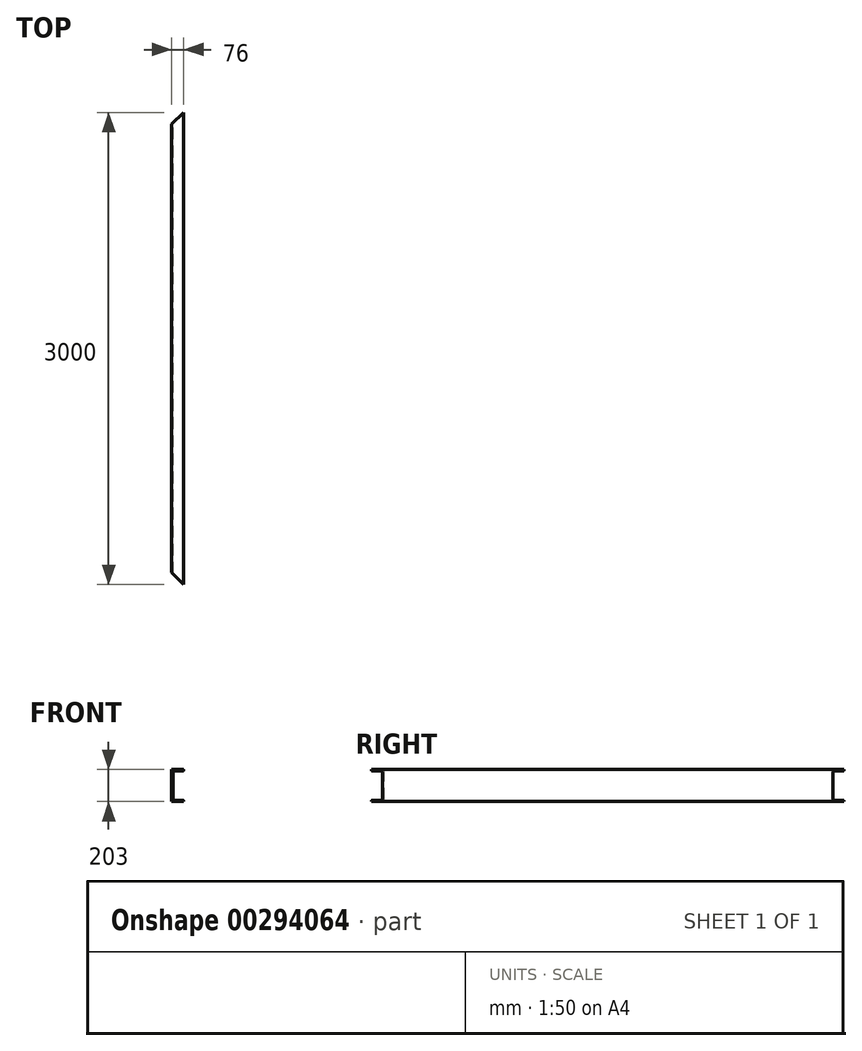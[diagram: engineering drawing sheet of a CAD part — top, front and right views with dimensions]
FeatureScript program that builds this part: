
annotation { "Feature Type Name" : "Feature", "Feature Type Description" : "" }
export const myFeature = defineFeature(function(context is Context, id is Id, definition is map)
    precondition{}
    {
        {
            var Q0;
            Q0=qCreatedBy(makeId("Front.planeOp"),FACE);
            var sketch = newSketch(context, id + "F0", { "sketchPlane" : qUnion([Q0])});
            skLineSegment(sketch, "E0", {"start": v(-38, 101.5) * mm, "end": v(-38, -101.5) * mm});
            skLineSegment(sketch, "E1", {"start": v(-38, -101.5) * mm, "end": v(38, -101.5) * mm});
            skLineSegment(sketch, "E2", {"start": v(38, -101.5) * mm, "end": v(38, -98.1) * mm});
            skArc(sketch, "E3", {"start": v(38, -98.1) * mm, "mid": v(36.63, -94.66) * mm, "end": v(33.27, -93.1) * mm});
            skLineSegment(sketch, "E4", {"start": v(33.27, -93.1) * mm, "end": v(-21.44, -90.17) * mm});
            skArc(sketch, "E5", {"start": v(-21.44, -90.17) * mm, "mid": v(-28.16, -87.07) * mm, "end": v(-30.9, -80.19) * mm});
            skLineSegment(sketch, "E6", {"start": v(-30.9, -80.19) * mm, "end": v(-30.9, 80.19) * mm});
            skArc(sketch, "E7", {"start": v(-30.9, 80.19) * mm, "mid": v(-28.16, 87.07) * mm, "end": v(-21.44, 90.17) * mm});
            skLineSegment(sketch, "E8", {"start": v(-21.44, 90.17) * mm, "end": v(33.27, 93.1) * mm});
            skArc(sketch, "E9", {"start": v(33.27, 93.1) * mm, "mid": v(36.63, 94.66) * mm, "end": v(38, 98.1) * mm});
            skLineSegment(sketch, "E10", {"start": v(38, 98.1) * mm, "end": v(38, 101.5) * mm});
            skLineSegment(sketch, "E11", {"start": v(38, 101.5) * mm, "end": v(-38, 101.5) * mm});
            skSolve(sketch);
        }
        {
            var Q0;
            Q0=makeQuery(id+"F0.imprint","IMPRINT",FACE,{"disambiguationData":[TD([[makeQuery(id+"F0.imprint","IMPRINT",EDGE,{"derivedFrom":sQuery(id+"F0.wireOp",EDGE,"E0")}),1.0]])]});
            extrude(context, id + "F1", {"entities" : qUnion([Q0]), "depth" : 3000 * mm});
        }
        {
            var Q0;
            Q0=qCreatedBy(makeId("Top.planeOp"),FACE);
            var sketch = newSketch(context, id + "F2", { "sketchPlane" : qUnion([Q0])});
            skLineSegment(sketch, "E12", {"start": v(-38, 0) * mm, "end": v(-38, -76) * mm});
            skLineSegment(sketch, "E13", {"start": v(38, 0) * mm, "end": v(-38, -76) * mm});
            skLineSegment(sketch, "E14", {"start": v(38, 0) * mm, "end": v(-38, 0) * mm});
            skLineSegment(sketch, "E15.MirrorCS", {"start": v(38, -3000) * mm, "end": v(-38, -3000) * mm});
            skLineSegment(sketch, "E16.MirrorCS", {"start": v(38, -3000) * mm, "end": v(-38, -2924) * mm});
            skLineSegment(sketch, "E17.MirrorCS", {"start": v(-38, -3000) * mm, "end": v(-38, -2924) * mm});
            skSolve(sketch);
        }
        {
            var Q0;
            Q0=makeQuery(id+"F2.imprint","IMPRINT",FACE,{"disambiguationData":[TD([[makeQuery(id+"F2.imprint","IMPRINT",EDGE,{"derivedFrom":sQuery(id+"F2.wireOp",EDGE,"E12")}),1.0]])]});
            var Q1;
            Q1=makeQuery(id+"F2.imprint","IMPRINT",FACE,{"disambiguationData":[TD([[makeQuery(id+"F2.imprint","IMPRINT",EDGE,{"derivedFrom":sQuery(id+"F2.wireOp",EDGE,"E15.MirrorCS")}),-1.0]])]});
            extrude(context, id + "F3", {"entities" : qUnion([Q0, Q1]), "operationType" : NewBodyOperationType.REMOVE, "depth" : 102 * mm, "hasSecondDirection" : true, "secondDirectionOppositeDirection" : true, "secondDirectionDepth" : 102 * mm});
        }
    });
